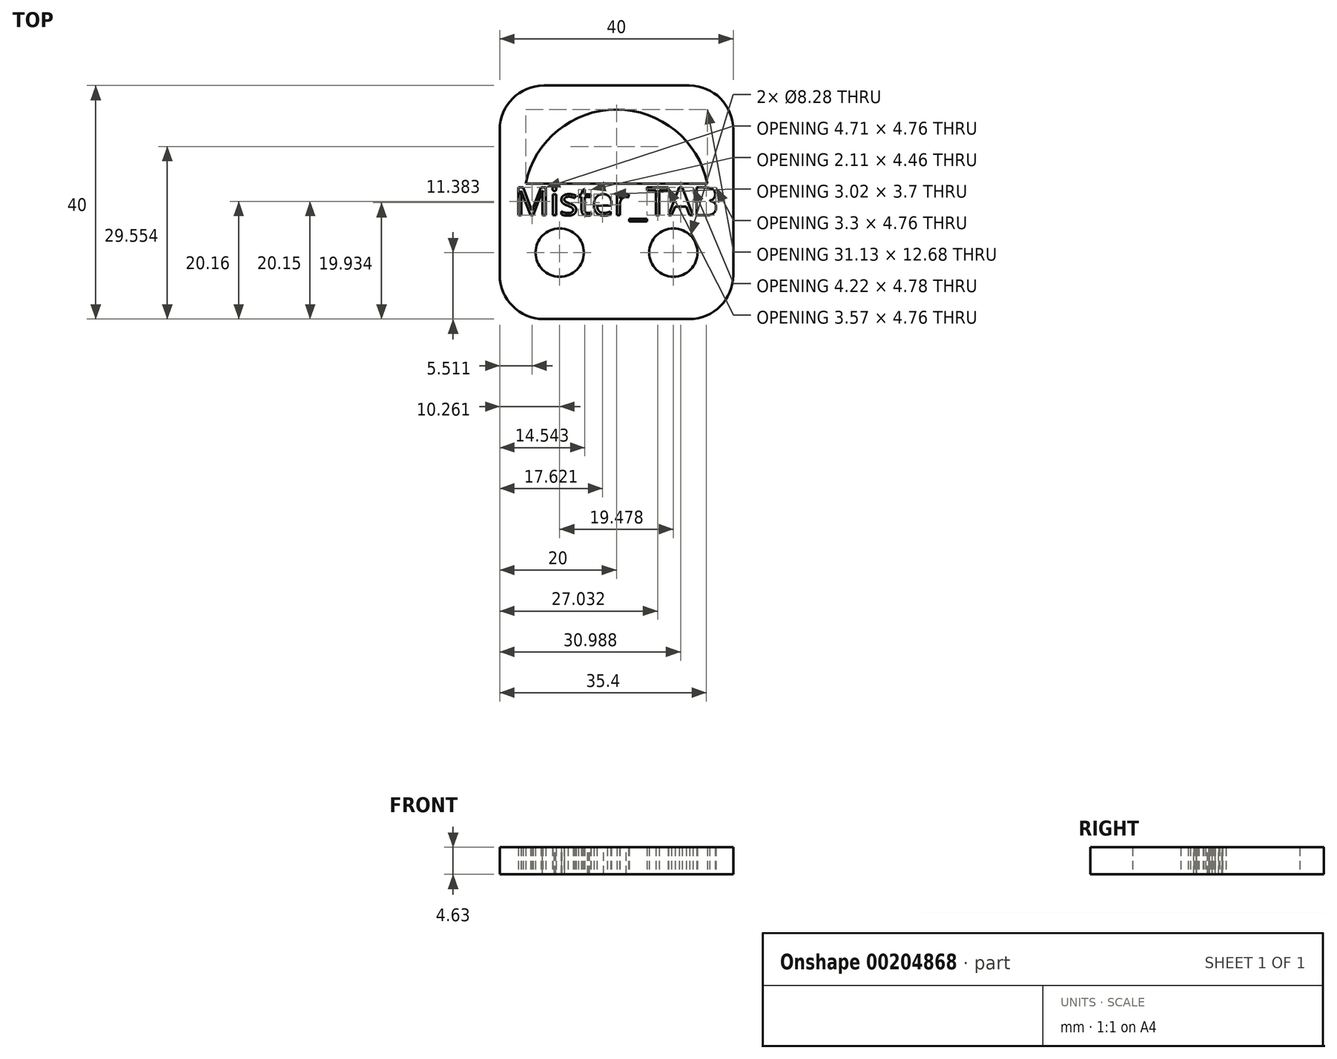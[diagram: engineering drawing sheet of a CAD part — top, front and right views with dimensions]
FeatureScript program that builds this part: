
annotation { "Feature Type Name" : "Feature", "Feature Type Description" : "" }
export const myFeature = defineFeature(function(context is Context, id is Id, definition is map)
    precondition{}
    {
        {
            var Q0;
            Q0=qCreatedBy(makeId("Top.planeOp"),FACE);
            var sketch = newSketch(context, id + "F0", { "sketchPlane" : qUnion([Q0])});
            skLineSegment(sketch, "E0.bottom", {"start": v(12.46, -20) * mm, "end": v(-12.46, -20) * mm});
            skLineSegment(sketch, "E0.top", {"start": v(12.46, 20) * mm, "end": v(-12.46, 20) * mm});
            skLineSegment(sketch, "E0.left", {"start": v(20, -12.46) * mm, "end": v(20, 12.46) * mm});
            skLineSegment(sketch, "E0.right", {"start": v(-20, -12.46) * mm, "end": v(-20, 12.46) * mm});
            skPoint(sketch, "E0.middle", {"position": v(0, 0) * mm});
            skPoint(sketch, "E1.visualSharp", {"position": v(20, 20) * mm});
            skArc(sketch, "E1.filletArc", {"start": v(20, 12.46) * mm, "mid": v(17.8, 17.8) * mm, "end": v(12.46, 20) * mm});
            skPoint(sketch, "E2.visualSharp", {"position": v(20, -20) * mm});
            skArc(sketch, "E2.filletArc", {"start": v(12.46, -20) * mm, "mid": v(17.8, -17.8) * mm, "end": v(20, -12.46) * mm});
            skPoint(sketch, "E3.visualSharp", {"position": v(-20, -20) * mm});
            skArc(sketch, "E3.filletArc", {"start": v(-20, -12.46) * mm, "mid": v(-17.8, -17.8) * mm, "end": v(-12.46, -20) * mm});
            skPoint(sketch, "E4.visualSharp", {"position": v(-20, 20) * mm});
            skArc(sketch, "E4.filletArc", {"start": v(-12.46, 20) * mm, "mid": v(-17.8, 17.8) * mm, "end": v(-20, 12.46) * mm});
            skLineSegment(sketch, "E5", {"start": v(0, 20) * mm, "end": v(0, -20) * mm, "construction": true});
            skLineSegment(sketch, "E6", {"start": v(20, 0) * mm, "end": v(-20, 0) * mm, "construction": true});
            skText(sketch, "E7", { "text": "Mister_TAB\n", "fontName": "OpenSans-Regular.ttf"});
            skLineSegment(sketch, "E8", {"start": v(-22.24, -9.82) * mm, "end": v(-21.34, -8.78) * mm});
            skLineSegment(sketch, "E9", {"start": v(21.65, -8.57) * mm, "end": v(22.24, -9.82) * mm});
            skLineSegment(sketch, "E10", {"start": v(-1.57, -18.38) * mm, "end": v(-1.57, -19.68) * mm});
            skLineSegment(sketch, "E11.MirrorCS", {"start": v(1.57, -18.38) * mm, "end": v(1.57, -19.68) * mm});
            skLineSegment(sketch, "E12", {"start": v(-20.17, -27.39) * mm, "end": v(-18.93, -28.33) * mm});
            skLineSegment(sketch, "E13", {"start": v(19.69, -28.34) * mm, "end": v(20.17, -27.39) * mm});
            skArc(sketch, "E14.trimOffspring", {"start": v(15.56, 3.22) * mm, "mid": v(0, 15.9) * mm, "end": v(-15.56, 3.22) * mm});
            skLineSegment(sketch, "E15", {"start": v(-15.56, 3.22) * mm, "end": v(15.56, 3.22) * mm});
            skCircle(sketch, "E16", {"center": v(-9.74, -8.62) * mm, "radius": 4.14 * mm});
            skCircle(sketch, "E17.MirrorC", {"center": v(9.74, -8.62) * mm, "radius": 4.14 * mm});
            const initialGuessF0  = {"E7": [-0.0175, -0.00223, 1, 0, 0.0048]};
            skSetInitialGuess(sketch, initialGuessF0);
            skSolve(sketch);
        }
        {
            var Q0;
            Q0=makeQuery(id+"F0.imprint","IMPRINT",FACE,{"disambiguationData":[TD([[makeQuery(id+"F0.imprint","IMPRINT",EDGE,{"derivedFrom":sQuery(id+"F0.wireOp",EDGE,"E0.bottom")}),-1.0]])]});
            extrude(context, id + "F1", {"entities" : qUnion([Q0]), "depth" : 4.63 * mm});
        }
    });
